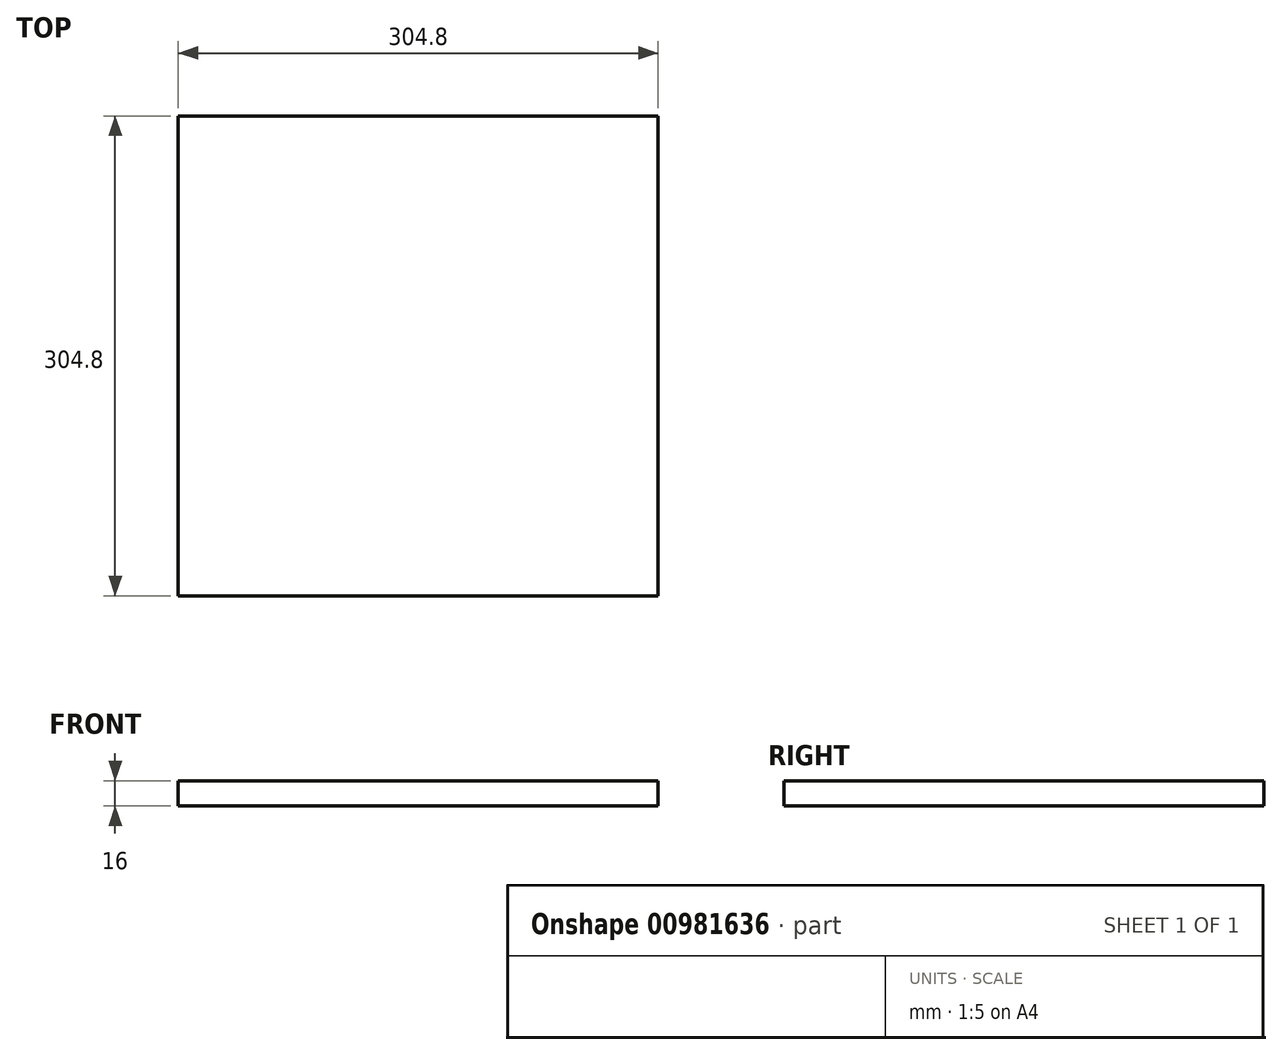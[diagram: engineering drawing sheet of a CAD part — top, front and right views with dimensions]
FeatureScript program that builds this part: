
annotation { "Feature Type Name" : "Feature", "Feature Type Description" : "" }
export const myFeature = defineFeature(function(context is Context, id is Id, definition is map)
    precondition{}
    {
        {
            var Q0;
            Q0=qCreatedBy(makeId("Top.planeOp"),FACE);
            var sketch = newSketch(context, id + "F0", { "sketchPlane" : qUnion([Q0])});
            skLineSegment(sketch, "E0.bottom", {"start": v(-145, 195.23) * mm, "end": v(159.8, 195.23) * mm});
            skLineSegment(sketch, "E0.top", {"start": v(-145, -109.57) * mm, "end": v(159.8, -109.57) * mm});
            skLineSegment(sketch, "E0.left", {"start": v(-145, 195.23) * mm, "end": v(-145, -109.57) * mm});
            skLineSegment(sketch, "E0.right", {"start": v(159.8, 195.23) * mm, "end": v(159.8, -109.57) * mm});
            skSolve(sketch);
        }
        {
            var Q0;
            Q0 = qSketchRegion(id + "F0", true);
            extrude(context, id + "F1", {"entities" : qUnion([Q0]), "depth" : 16 * mm, "offsetDistance" : 25 * mm});
        }
    });
